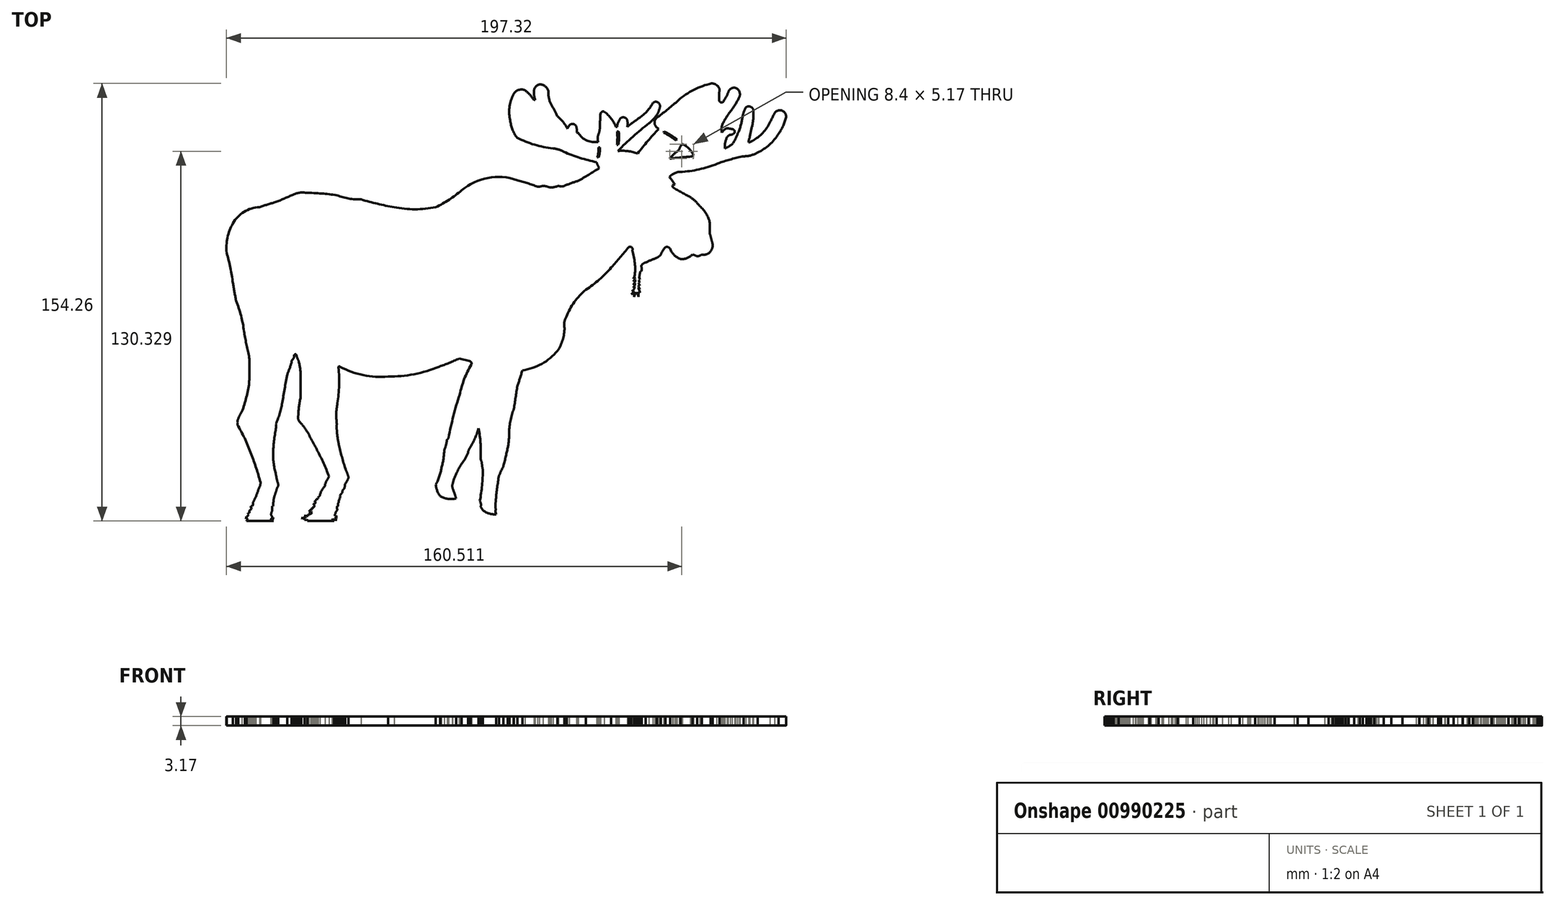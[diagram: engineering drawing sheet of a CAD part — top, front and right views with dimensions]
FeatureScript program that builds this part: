
annotation { "Feature Type Name" : "Feature", "Feature Type Description" : "" }
export const myFeature = defineFeature(function(context is Context, id is Id, definition is map)
    precondition{}
    {
        {
            var Q0;
            Q0=qCreatedBy(makeId("Top.planeOp"),FACE);
            var sketch = newSketch(context, id + "F0", { "sketchPlane" : qUnion([Q0])});
            skArc(sketch, "E0", {"start": v(147.27, 120.2) * mm, "mid": v(137.02, 120.96) * mm, "end": v(127.73, 116.58) * mm});
            skArc(sketch, "E1", {"start": v(118.62, 110.64) * mm, "mid": v(123.37, 113.31) * mm, "end": v(127.73, 116.58) * mm});
            skArc(sketch, "E2", {"start": v(103.93, 110.64) * mm, "mid": v(111.28, 109.9) * mm, "end": v(118.62, 110.64) * mm});
            skArc(sketch, "E3", {"start": v(92.29, 113.4) * mm, "mid": v(98.07, 111.84) * mm, "end": v(103.93, 110.64) * mm});
            skArc(sketch, "E4", {"start": v(83.82, 114.84) * mm, "mid": v(87.98, 113.66) * mm, "end": v(92.29, 113.4) * mm});
            skArc(sketch, "E5", {"start": v(83.82, 114.84) * mm, "mid": v(78.38, 115.45) * mm, "end": v(72.9, 115.7) * mm});
            skArc(sketch, "E6", {"start": v(72.9, 115.7) * mm, "mid": v(70.3, 115.7) * mm, "end": v(67.84, 114.84) * mm});
            skArc(sketch, "E7", {"start": v(61.98, 112.38) * mm, "mid": v(64.93, 113.56) * mm, "end": v(67.84, 114.84) * mm});
            skArc(sketch, "E8", {"start": v(61.98, 112.38) * mm, "mid": v(59.21, 111.56) * mm, "end": v(56.48, 110.64) * mm});
            skArc(sketch, "E9", {"start": v(56.48, 110.64) * mm, "mid": v(51.05, 109) * mm, "end": v(47.1, 104.92) * mm});
            skArc(sketch, "E10", {"start": v(47.1, 104.92) * mm, "mid": v(45.23, 99.89) * mm, "end": v(44.92, 94.53) * mm});
            skArc(sketch, "E11", {"start": v(47.1, 83.95) * mm, "mid": v(46.2, 89.28) * mm, "end": v(44.92, 94.53) * mm});
            skArc(sketch, "E12", {"start": v(47.1, 83.95) * mm, "mid": v(47.65, 80.8) * mm, "end": v(48.2, 77.66) * mm});
            skArc(sketch, "E13", {"start": v(51.03, 66.86) * mm, "mid": v(49.97, 72.36) * mm, "end": v(48.2, 77.66) * mm});
            skArc(sketch, "E14", {"start": v(51.03, 66.86) * mm, "mid": v(51.84, 62.51) * mm, "end": v(52.85, 58.2) * mm});
            skArc(sketch, "E15", {"start": v(52.85, 48.63) * mm, "mid": v(52.95, 53.42) * mm, "end": v(52.85, 58.2) * mm});
            skArc(sketch, "E16", {"start": v(50.3, 38.56) * mm, "mid": v(51.84, 43.53) * mm, "end": v(52.85, 48.63) * mm});
            skArc(sketch, "E17", {"start": v(50.3, 38.56) * mm, "mid": v(49.54, 37.31) * mm, "end": v(48.98, 35.96) * mm});
            skArc(sketch, "E18", {"start": v(48.98, 35.96) * mm, "mid": v(48.68, 34.67) * mm, "end": v(48.98, 33.37) * mm});
            skArc(sketch, "E19", {"start": v(53.58, 23.48) * mm, "mid": v(51.53, 28.54) * mm, "end": v(48.98, 33.37) * mm});
            skArc(sketch, "E20", {"start": v(56.82, 13.59) * mm, "mid": v(55.35, 18.58) * mm, "end": v(53.58, 23.48) * mm});
            skArc(sketch, "E21", {"start": v(56.48, 11.9) * mm, "mid": v(56.77, 12.72) * mm, "end": v(56.82, 13.59) * mm});
            skArc(sketch, "E22", {"start": v(56.48, 11.9) * mm, "mid": v(55.79, 10.14) * mm, "end": v(55.2, 8.34) * mm});
            skLineSegment(sketch, "E23", {"start": v(55.2, 8.34) * mm, "end": v(54.71, 7.8) * mm});
            skLineSegment(sketch, "E24", {"start": v(54.71, 7.8) * mm, "end": v(54.71, 7.32) * mm});
            skLineSegment(sketch, "E25", {"start": v(54.71, 7.32) * mm, "end": v(54.14, 6.57) * mm});
            skLineSegment(sketch, "E26", {"start": v(54.14, 6.57) * mm, "end": v(54.14, 6.18) * mm});
            skLineSegment(sketch, "E27", {"start": v(54.14, 6.18) * mm, "end": v(54.14, 5.68) * mm});
            skLineSegment(sketch, "E28", {"start": v(54.14, 5.68) * mm, "end": v(53.9, 5.27) * mm});
            skLineSegment(sketch, "E29", {"start": v(53.9, 5.27) * mm, "end": v(53.4, 5.27) * mm});
            skLineSegment(sketch, "E30", {"start": v(53.4, 5.27) * mm, "end": v(53.4, 5) * mm});
            skLineSegment(sketch, "E31", {"start": v(53.4, 5) * mm, "end": v(53.73, 4.26) * mm});
            skLineSegment(sketch, "E32", {"start": v(53.73, 4.26) * mm, "end": v(52.96, 3.72) * mm});
            skLineSegment(sketch, "E33", {"start": v(52.96, 3.72) * mm, "end": v(52.96, 2.8) * mm});
            skLineSegment(sketch, "E34", {"start": v(52.96, 2.8) * mm, "end": v(52.48, 2.8) * mm});
            skLineSegment(sketch, "E35", {"start": v(52.48, 2.8) * mm, "end": v(52.4, 2.5) * mm});
            skLineSegment(sketch, "E36", {"start": v(52.4, 2.5) * mm, "end": v(52.65, 2.15) * mm});
            skLineSegment(sketch, "E37", {"start": v(52.65, 2.15) * mm, "end": v(52.29, 1.8) * mm});
            skLineSegment(sketch, "E38", {"start": v(52.29, 1.8) * mm, "end": v(52.01, 1.59) * mm});
            skLineSegment(sketch, "E39", {"start": v(52.01, 1.59) * mm, "end": v(51.87, 1.1) * mm});
            skLineSegment(sketch, "E40", {"start": v(51.87, 1.1) * mm, "end": v(51.47, 1.1) * mm});
            skLineSegment(sketch, "E41", {"start": v(51.47, 1.1) * mm, "end": v(52.12, 0.85) * mm});
            skLineSegment(sketch, "E42", {"start": v(52.12, 0.85) * mm, "end": v(52.12, 0.4) * mm});
            skLineSegment(sketch, "E43", {"start": v(52.12, 0.4) * mm, "end": v(52.04, 0.2) * mm});
            skLineSegment(sketch, "E44", {"start": v(52.04, 0.2) * mm, "end": v(51.86, 0.2) * mm});
            skLineSegment(sketch, "E45", {"start": v(51.86, 0.2) * mm, "end": v(51.86, 0) * mm});
            skLineSegment(sketch, "E46", {"start": v(51.86, 0) * mm, "end": v(61.45, 0) * mm});
            skLineSegment(sketch, "E47", {"start": v(61.45, 0) * mm, "end": v(60.66, 0.2) * mm});
            skArc(sketch, "E48", {"start": v(60.86, 0.86) * mm, "mid": v(60.5, 0.6) * mm, "end": v(60.66, 0.2) * mm});
            skArc(sketch, "E49", {"start": v(60.86, 0.86) * mm, "mid": v(61.23, 0.8) * mm, "end": v(61.6, 0.77) * mm});
            skArc(sketch, "E50", {"start": v(61.6, 0.77) * mm, "mid": v(61.3, 1) * mm, "end": v(61, 1.21) * mm});
            skArc(sketch, "E51", {"start": v(60.86, 1.81) * mm, "mid": v(60.9, 1.5) * mm, "end": v(61, 1.21) * mm});
            skArc(sketch, "E52", {"start": v(60.66, 1.89) * mm, "mid": v(60.75, 1.81) * mm, "end": v(60.86, 1.81) * mm});
            skArc(sketch, "E53", {"start": v(61, 3.62) * mm, "mid": v(60.65, 2.79) * mm, "end": v(60.66, 1.89) * mm});
            skArc(sketch, "E54", {"start": v(61, 5.23) * mm, "mid": v(60.98, 4.42) * mm, "end": v(61, 3.62) * mm});
            skArc(sketch, "E55", {"start": v(61.6, 8.16) * mm, "mid": v(61.39, 6.7) * mm, "end": v(61.38, 5.23) * mm});
            skLineSegment(sketch, "E56", {"start": v(61.38, 5.23) * mm, "end": v(61, 5.23) * mm});
            skArc(sketch, "E57", {"start": v(62.5, 10.85) * mm, "mid": v(62.03, 9.51) * mm, "end": v(61.6, 8.16) * mm});
            skArc(sketch, "E58", {"start": v(63.08, 12.3) * mm, "mid": v(62.73, 11.68) * mm, "end": v(62.5, 11.02) * mm});
            skLineSegment(sketch, "E59", {"start": v(62.5, 10.85) * mm, "end": v(62.5, 11.02) * mm});
            skArc(sketch, "E60", {"start": v(63.08, 12.3) * mm, "mid": v(63.1, 12.9) * mm, "end": v(62.91, 13.49) * mm});
            skArc(sketch, "E61", {"start": v(62.27, 16.4) * mm, "mid": v(62.55, 14.93) * mm, "end": v(62.91, 13.49) * mm});
            skArc(sketch, "E62", {"start": v(61.27, 23.8) * mm, "mid": v(61.52, 20.06) * mm, "end": v(62.27, 16.4) * mm});
            skArc(sketch, "E63", {"start": v(62.27, 32.62) * mm, "mid": v(61.63, 28.22) * mm, "end": v(61.27, 23.8) * mm});
            skArc(sketch, "E64", {"start": v(62.27, 32.62) * mm, "mid": v(62.34, 33.38) * mm, "end": v(62.27, 34.14) * mm});
            skArc(sketch, "E65", {"start": v(62.27, 34.14) * mm, "mid": v(63.6, 37.84) * mm, "end": v(64.5, 41.66) * mm});
            skArc(sketch, "E66", {"start": v(66.24, 51.53) * mm, "mid": v(65.35, 46.6) * mm, "end": v(64.5, 41.66) * mm});
            skArc(sketch, "E67", {"start": v(66.24, 51.53) * mm, "mid": v(67.04, 53.64) * mm, "end": v(67.79, 55.77) * mm});
            skArc(sketch, "E68", {"start": v(67.79, 56.5) * mm, "mid": v(67.76, 56.13) * mm, "end": v(67.79, 55.77) * mm});
            skArc(sketch, "E69", {"start": v(67.79, 56.5) * mm, "mid": v(68.25, 57.03) * mm, "end": v(68.65, 57.61) * mm});
            skArc(sketch, "E70", {"start": v(69.43, 58.68) * mm, "mid": v(68.92, 58.7) * mm, "end": v(68.7, 58.25) * mm});
            skArc(sketch, "E71", {"start": v(68.7, 58.25) * mm, "mid": v(68.63, 57.93) * mm, "end": v(68.65, 57.61) * mm});
            skArc(sketch, "E72", {"start": v(69.43, 58.68) * mm, "mid": v(69.81, 57.5) * mm, "end": v(70.3, 56.38) * mm});
            skArc(sketch, "E73", {"start": v(71.02, 50.46) * mm, "mid": v(70.86, 53.44) * mm, "end": v(70.3, 56.38) * mm});
            skLineSegment(sketch, "E74", {"start": v(71.02, 50.46) * mm, "end": v(71.02, 43.72) * mm});
            skArc(sketch, "E75", {"start": v(71.02, 43.72) * mm, "mid": v(70.44, 40.5) * mm, "end": v(70.15, 37.25) * mm});
            skArc(sketch, "E76", {"start": v(70.15, 37.25) * mm, "mid": v(70.1, 36.07) * mm, "end": v(70.62, 35) * mm});
            skArc(sketch, "E77", {"start": v(72.94, 32.1) * mm, "mid": v(71.84, 33.6) * mm, "end": v(70.62, 35) * mm});
            skArc(sketch, "E78", {"start": v(76.86, 24.83) * mm, "mid": v(74.95, 28.5) * mm, "end": v(72.94, 32.1) * mm});
            skArc(sketch, "E79", {"start": v(80.96, 15.74) * mm, "mid": v(79.08, 20.36) * mm, "end": v(76.86, 24.83) * mm});
            skArc(sketch, "E80", {"start": v(79.55, 12.91) * mm, "mid": v(80.27, 14.32) * mm, "end": v(80.96, 15.74) * mm});
            skArc(sketch, "E81", {"start": v(79.64, 12.32) * mm, "mid": v(78.43, 10.81) * mm, "end": v(77.77, 9) * mm});
            skLineSegment(sketch, "E82", {"start": v(79.64, 12.32) * mm, "end": v(79.55, 12.91) * mm});
            skArc(sketch, "E83", {"start": v(77.08, 8.3) * mm, "mid": v(77.5, 8.59) * mm, "end": v(77.77, 9) * mm});
            skArc(sketch, "E84", {"start": v(76.55, 7.75) * mm, "mid": v(76.86, 7.7) * mm, "end": v(77.17, 7.78) * mm});
            skArc(sketch, "E85", {"start": v(75.82, 6.86) * mm, "mid": v(76.32, 7.2) * mm, "end": v(76.55, 7.75) * mm});
            skArc(sketch, "E86", {"start": v(76.24, 6.51) * mm, "mid": v(76.08, 6.74) * mm, "end": v(75.82, 6.86) * mm});
            skArc(sketch, "E87", {"start": v(75.45, 6) * mm, "mid": v(75.96, 6.08) * mm, "end": v(76.24, 6.51) * mm});
            skArc(sketch, "E88", {"start": v(75.82, 5.35) * mm, "mid": v(75.7, 5.72) * mm, "end": v(75.45, 6) * mm});
            skArc(sketch, "E89", {"start": v(75.45, 4.72) * mm, "mid": v(75.76, 4.96) * mm, "end": v(75.82, 5.35) * mm});
            skArc(sketch, "E90", {"start": v(74.98, 4.72) * mm, "mid": v(75.21, 4.64) * mm, "end": v(75.45, 4.72) * mm});
            skArc(sketch, "E91", {"start": v(74.98, 4.06) * mm, "mid": v(75.07, 4.4) * mm, "end": v(74.98, 4.72) * mm});
            skLineSegment(sketch, "E92", {"start": v(74.98, 4.06) * mm, "end": v(74.47, 3.96) * mm});
            skLineSegment(sketch, "E93", {"start": v(74.47, 3.96) * mm, "end": v(73.9, 3.36) * mm});
            skLineSegment(sketch, "E94", {"start": v(73.9, 3.36) * mm, "end": v(74.81, 3.22) * mm});
            skLineSegment(sketch, "E95", {"start": v(74.81, 3.22) * mm, "end": v(74.98, 2.88) * mm});
            skLineSegment(sketch, "E96", {"start": v(74.98, 2.88) * mm, "end": v(74.73, 2.66) * mm});
            skLineSegment(sketch, "E97", {"start": v(74.73, 2.66) * mm, "end": v(74.47, 2.4) * mm});
            skLineSegment(sketch, "E98", {"start": v(74.47, 2.4) * mm, "end": v(73.82, 2.4) * mm});
            skLineSegment(sketch, "E99", {"start": v(73.82, 2.4) * mm, "end": v(73.58, 1.75) * mm});
            skLineSegment(sketch, "E100", {"start": v(73.58, 1.75) * mm, "end": v(73.07, 1.75) * mm});
            skLineSegment(sketch, "E101", {"start": v(73.07, 1.75) * mm, "end": v(72.27, 1.75) * mm});
            skLineSegment(sketch, "E102", {"start": v(72.27, 1.75) * mm, "end": v(72.92, 1.26) * mm});
            skLineSegment(sketch, "E103", {"start": v(72.92, 1.26) * mm, "end": v(72.75, 1.04) * mm});
            skLineSegment(sketch, "E104", {"start": v(72.75, 1.04) * mm, "end": v(72.34, 1.09) * mm});
            skLineSegment(sketch, "E105", {"start": v(72.34, 1.09) * mm, "end": v(71.3, 1.09) * mm});
            skLineSegment(sketch, "E106", {"start": v(71.3, 1.09) * mm, "end": v(72.43, 0.71) * mm});
            skLineSegment(sketch, "E107", {"start": v(72.43, 0.71) * mm, "end": v(72.43, 0.45) * mm});
            skLineSegment(sketch, "E108", {"start": v(72.43, 0.45) * mm, "end": v(73.6, 0.28) * mm});
            skLineSegment(sketch, "E109", {"start": v(73.6, 0.28) * mm, "end": v(73.4, 0) * mm});
            skLineSegment(sketch, "E110", {"start": v(73.4, 0) * mm, "end": v(82.74, 0) * mm});
            skLineSegment(sketch, "E111", {"start": v(77.17, 7.78) * mm, "end": v(77.08, 8.3) * mm});
            skLineSegment(sketch, "E112", {"start": v(82.74, 0) * mm, "end": v(82.13, 0.2) * mm});
            skLineSegment(sketch, "E113", {"start": v(82.13, 0.2) * mm, "end": v(81.98, 0.38) * mm});
            skLineSegment(sketch, "E114", {"start": v(81.98, 0.38) * mm, "end": v(82.29, 0.63) * mm});
            skLineSegment(sketch, "E115", {"start": v(82.29, 0.63) * mm, "end": v(82.95, 0.42) * mm});
            skLineSegment(sketch, "E116", {"start": v(82.95, 0.42) * mm, "end": v(83.3, 0.42) * mm});
            skLineSegment(sketch, "E117", {"start": v(83.3, 0.42) * mm, "end": v(83.78, 0.42) * mm});
            skLineSegment(sketch, "E118", {"start": v(83.78, 0.42) * mm, "end": v(83.26, 0.64) * mm});
            skLineSegment(sketch, "E119", {"start": v(83.26, 0.64) * mm, "end": v(83.26, 1.24) * mm});
            skLineSegment(sketch, "E120", {"start": v(83.26, 1.24) * mm, "end": v(83.86, 1.36) * mm});
            skLineSegment(sketch, "E121", {"start": v(83.86, 1.36) * mm, "end": v(83.43, 1.61) * mm});
            skLineSegment(sketch, "E122", {"start": v(83.43, 1.61) * mm, "end": v(83.13, 1.8) * mm});
            skLineSegment(sketch, "E123", {"start": v(83.13, 1.8) * mm, "end": v(83.03, 2.12) * mm});
            skLineSegment(sketch, "E124", {"start": v(83.03, 2.12) * mm, "end": v(83.07, 2.32) * mm});
            skLineSegment(sketch, "E125", {"start": v(83.07, 2.32) * mm, "end": v(83.33, 2.55) * mm});
            skLineSegment(sketch, "E126", {"start": v(83.33, 2.55) * mm, "end": v(83.33, 3.08) * mm});
            skLineSegment(sketch, "E127", {"start": v(83.33, 3.08) * mm, "end": v(83.98, 3.88) * mm});
            skArc(sketch, "E128", {"start": v(83.8, 5.06) * mm, "mid": v(83.8, 4.46) * mm, "end": v(83.98, 3.88) * mm});
            skArc(sketch, "E129", {"start": v(84.27, 5.29) * mm, "mid": v(84.01, 5.22) * mm, "end": v(83.8, 5.06) * mm});
            skArc(sketch, "E130", {"start": v(84.5, 6.68) * mm, "mid": v(84.17, 6.02) * mm, "end": v(84.27, 5.29) * mm});
            skArc(sketch, "E131", {"start": v(84.7, 7.61) * mm, "mid": v(84.48, 7.17) * mm, "end": v(84.5, 6.68) * mm});
            skArc(sketch, "E132", {"start": v(84.5, 7.83) * mm, "mid": v(84.83, 8.1) * mm, "end": v(85.08, 8.43) * mm});
            skArc(sketch, "E133", {"start": v(84.75, 8.9) * mm, "mid": v(85.25, 9.44) * mm, "end": v(85.69, 10.03) * mm});
            skLineSegment(sketch, "E134", {"start": v(84.7, 7.61) * mm, "end": v(84.5, 7.83) * mm});
            skLineSegment(sketch, "E135", {"start": v(85.08, 8.43) * mm, "end": v(84.75, 8.9) * mm});
            skArc(sketch, "E136", {"start": v(86.05, 11.12) * mm, "mid": v(85.75, 10.6) * mm, "end": v(85.69, 10.03) * mm});
            skArc(sketch, "E137", {"start": v(86.05, 11.12) * mm, "mid": v(86.33, 11.38) * mm, "end": v(86.45, 11.76) * mm});
            skArc(sketch, "E138", {"start": v(86.45, 11.76) * mm, "mid": v(86.62, 12.37) * mm, "end": v(86.65, 13.01) * mm});
            skArc(sketch, "E139", {"start": v(86.65, 13.01) * mm, "mid": v(87.39, 14.17) * mm, "end": v(87.91, 15.44) * mm});
            skArc(sketch, "E140", {"start": v(87.91, 15.44) * mm, "mid": v(87.37, 16.9) * mm, "end": v(86.8, 18.34) * mm});
            skArc(sketch, "E141", {"start": v(84.45, 27) * mm, "mid": v(85.53, 22.64) * mm, "end": v(86.8, 18.34) * mm});
            skArc(sketch, "E142", {"start": v(83.77, 32.01) * mm, "mid": v(84, 29.5) * mm, "end": v(84.45, 27) * mm});
            skArc(sketch, "E143", {"start": v(83.77, 34.2) * mm, "mid": v(83.65, 33.1) * mm, "end": v(83.77, 32.01) * mm});
            skArc(sketch, "E144", {"start": v(83.55, 38.12) * mm, "mid": v(83.59, 36.15) * mm, "end": v(83.77, 34.2) * mm});
            skArc(sketch, "E145", {"start": v(83.97, 41.5) * mm, "mid": v(83.72, 39.82) * mm, "end": v(83.55, 38.12) * mm});
            skArc(sketch, "E146", {"start": v(83.97, 41.5) * mm, "mid": v(84.55, 47.77) * mm, "end": v(84.33, 54.05) * mm});
            skArc(sketch, "E147", {"start": v(84.82, 54.41) * mm, "mid": v(84.42, 54.45) * mm, "end": v(84.33, 54.05) * mm});
            skArc(sketch, "E148", {"start": v(84.82, 54.41) * mm, "mid": v(93.08, 51.4) * mm, "end": v(101.86, 50.91) * mm});
            skArc(sketch, "E149", {"start": v(101.86, 50.91) * mm, "mid": v(111.02, 51.74) * mm, "end": v(119.83, 54.41) * mm});
            skArc(sketch, "E150", {"start": v(119.83, 54.41) * mm, "mid": v(123.38, 55.75) * mm, "end": v(126.85, 57.27) * mm});
            skLineSegment(sketch, "E151", {"start": v(126.85, 57.27) * mm, "end": v(130.57, 56.37) * mm});
            skArc(sketch, "E152", {"start": v(131.15, 55.1) * mm, "mid": v(131.17, 55.88) * mm, "end": v(130.57, 56.37) * mm});
            skArc(sketch, "E153", {"start": v(131.15, 55.1) * mm, "mid": v(128.68, 50) * mm, "end": v(127.05, 44.56) * mm});
            skArc(sketch, "E154", {"start": v(127.05, 44.56) * mm, "mid": v(124.85, 37.02) * mm, "end": v(123.14, 29.35) * mm});
            skArc(sketch, "E155", {"start": v(121.64, 25) * mm, "mid": v(122.24, 26.8) * mm, "end": v(122.61, 28.67) * mm});
            skArc(sketch, "E156", {"start": v(120.7, 18.85) * mm, "mid": v(121.33, 21.9) * mm, "end": v(121.64, 25) * mm});
            skArc(sketch, "E157", {"start": v(122.61, 28.67) * mm, "mid": v(122.93, 28.97) * mm, "end": v(123.14, 29.35) * mm});
            skArc(sketch, "E158", {"start": v(118.64, 12.8) * mm, "mid": v(119.91, 15.74) * mm, "end": v(120.7, 18.85) * mm});
            skArc(sketch, "E159", {"start": v(118.64, 12.8) * mm, "mid": v(119.14, 10.62) * mm, "end": v(120.25, 8.67) * mm});
            skArc(sketch, "E160", {"start": v(120.25, 8.67) * mm, "mid": v(122.94, 7.77) * mm, "end": v(125.78, 7.93) * mm});
            skArc(sketch, "E161", {"start": v(125.78, 7.93) * mm, "mid": v(125.28, 9.57) * mm, "end": v(124.7, 11.18) * mm});
            skArc(sketch, "E162", {"start": v(124.53, 13.02) * mm, "mid": v(124.48, 12.1) * mm, "end": v(124.7, 11.18) * mm});
            skArc(sketch, "E163", {"start": v(127.73, 20.17) * mm, "mid": v(125.88, 16.7) * mm, "end": v(124.53, 13.02) * mm});
            skArc(sketch, "E164", {"start": v(127.73, 20.17) * mm, "mid": v(129.02, 22) * mm, "end": v(129.98, 24.04) * mm});
            skArc(sketch, "E165", {"start": v(130.92, 26.14) * mm, "mid": v(130.34, 25.14) * mm, "end": v(129.98, 24.04) * mm});
            skArc(sketch, "E166", {"start": v(130.92, 26.14) * mm, "mid": v(132.54, 29.31) * mm, "end": v(133.77, 32.66) * mm});
            skArc(sketch, "E167", {"start": v(134.45, 22.58) * mm, "mid": v(134.4, 27.64) * mm, "end": v(133.77, 32.66) * mm});
            skArc(sketch, "E168", {"start": v(134.45, 22.58) * mm, "mid": v(134.52, 21.65) * mm, "end": v(134.86, 20.78) * mm});
            skArc(sketch, "E169", {"start": v(134.86, 20.78) * mm, "mid": v(134.98, 19.42) * mm, "end": v(135.23, 18.07) * mm});
            skArc(sketch, "E170", {"start": v(134.15, 7.1) * mm, "mid": v(134.97, 12.55) * mm, "end": v(135.23, 18.07) * mm});
            skArc(sketch, "E171", {"start": v(134.45, 4.93) * mm, "mid": v(134.54, 6.04) * mm, "end": v(134.15, 7.1) * mm});
            skLineSegment(sketch, "E172", {"start": v(134.45, 4.93) * mm, "end": v(135.27, 3.8) * mm});
            skArc(sketch, "E173", {"start": v(135.27, 3.8) * mm, "mid": v(137.43, 2.63) * mm, "end": v(139.88, 2.33) * mm});
            skLineSegment(sketch, "E174", {"start": v(139.88, 2.33) * mm, "end": v(139.62, 3.24) * mm});
            skArc(sketch, "E175", {"start": v(139.62, 3.24) * mm, "mid": v(139.75, 4.1) * mm, "end": v(139.62, 4.95) * mm});
            skArc(sketch, "E176", {"start": v(139.84, 7.68) * mm, "mid": v(139.73, 6.31) * mm, "end": v(139.62, 4.95) * mm});
            skArc(sketch, "E177", {"start": v(140.95, 15.96) * mm, "mid": v(140.28, 11.83) * mm, "end": v(139.84, 7.68) * mm});
            skArc(sketch, "E178", {"start": v(142.43, 19.07) * mm, "mid": v(141.64, 17.54) * mm, "end": v(140.95, 15.96) * mm});
            skArc(sketch, "E179", {"start": v(142.43, 19.07) * mm, "mid": v(143.25, 22.43) * mm, "end": v(144.02, 25.8) * mm});
            skArc(sketch, "E180", {"start": v(144.02, 25.8) * mm, "mid": v(144.4, 28.52) * mm, "end": v(144.53, 31.26) * mm});
            skArc(sketch, "E181", {"start": v(146.2, 39.56) * mm, "mid": v(144.97, 35.49) * mm, "end": v(144.53, 31.26) * mm});
            skArc(sketch, "E182", {"start": v(147.42, 47.62) * mm, "mid": v(146.8, 43.6) * mm, "end": v(146.2, 39.56) * mm});
            skArc(sketch, "E183", {"start": v(147.42, 47.62) * mm, "mid": v(148.34, 50.36) * mm, "end": v(149.15, 53.14) * mm});
            skArc(sketch, "E184", {"start": v(149.15, 53.14) * mm, "mid": v(156, 55.38) * mm, "end": v(161.55, 59.97) * mm});
            skArc(sketch, "E185", {"start": v(161.55, 59.97) * mm, "mid": v(163.4, 63.84) * mm, "end": v(164.01, 68.09) * mm});
            skArc(sketch, "E186", {"start": v(164.7, 71.96) * mm, "mid": v(163.96, 70.1) * mm, "end": v(164.01, 68.09) * mm});
            skArc(sketch, "E187", {"start": v(171.53, 81.48) * mm, "mid": v(167.48, 77.18) * mm, "end": v(164.7, 71.96) * mm});
            skArc(sketch, "E188", {"start": v(171.53, 81.48) * mm, "mid": v(176.29, 85.12) * mm, "end": v(180.5, 89.37) * mm});
            skArc(sketch, "E189", {"start": v(180.5, 89.37) * mm, "mid": v(183.64, 92.92) * mm, "end": v(186.66, 96.57) * mm});
            skArc(sketch, "E190", {"start": v(187.94, 95.43) * mm, "mid": v(187.74, 96.5) * mm, "end": v(186.66, 96.57) * mm});
            skArc(sketch, "E191", {"start": v(188.75, 86.27) * mm, "mid": v(188.83, 90.9) * mm, "end": v(187.94, 95.43) * mm});
            skLineSegment(sketch, "E192", {"start": v(188.75, 86.27) * mm, "end": v(188.3, 85.34) * mm});
            skLineSegment(sketch, "E193", {"start": v(188.3, 85.34) * mm, "end": v(188.75, 85.92) * mm});
            skLineSegment(sketch, "E194", {"start": v(188.75, 85.92) * mm, "end": v(188.98, 85.38) * mm});
            skLineSegment(sketch, "E195", {"start": v(188.98, 85.38) * mm, "end": v(188.31, 84.4) * mm});
            skLineSegment(sketch, "E196", {"start": v(188.31, 84.4) * mm, "end": v(188.98, 84.93) * mm});
            skLineSegment(sketch, "E197", {"start": v(188.98, 84.93) * mm, "end": v(188.98, 84.4) * mm});
            skLineSegment(sketch, "E198", {"start": v(188.98, 84.4) * mm, "end": v(188.22, 83.23) * mm});
            skLineSegment(sketch, "E199", {"start": v(188.22, 83.23) * mm, "end": v(189.02, 83.9) * mm});
            skLineSegment(sketch, "E200", {"start": v(189.02, 83.9) * mm, "end": v(188.75, 82.95) * mm});
            skLineSegment(sketch, "E201", {"start": v(188.75, 82.95) * mm, "end": v(188.15, 82.2) * mm});
            skLineSegment(sketch, "E202", {"start": v(188.15, 82.2) * mm, "end": v(188.75, 82.68) * mm});
            skArc(sketch, "E203", {"start": v(187.8, 81.04) * mm, "mid": v(188.5, 81.73) * mm, "end": v(188.75, 82.68) * mm});
            skArc(sketch, "E204", {"start": v(187.8, 81.04) * mm, "mid": v(188.1, 81.1) * mm, "end": v(188.39, 81.2) * mm});
            skArc(sketch, "E205", {"start": v(187.6, 79.95) * mm, "mid": v(188.1, 80.51) * mm, "end": v(188.39, 81.2) * mm});
            skArc(sketch, "E206", {"start": v(187.6, 79.95) * mm, "mid": v(188.2, 80.28) * mm, "end": v(188.61, 80.82) * mm});
            skArc(sketch, "E207", {"start": v(188.61, 79.04) * mm, "mid": v(188.63, 79.93) * mm, "end": v(188.61, 80.82) * mm});
            skArc(sketch, "E208", {"start": v(189.32, 80.5) * mm, "mid": v(188.88, 79.82) * mm, "end": v(188.61, 79.04) * mm});
            skArc(sketch, "E209", {"start": v(190.1, 79.04) * mm, "mid": v(189.83, 79.84) * mm, "end": v(189.32, 80.5) * mm});
            skArc(sketch, "E210", {"start": v(190.1, 79.04) * mm, "mid": v(190.13, 79.93) * mm, "end": v(190.1, 80.82) * mm});
            skArc(sketch, "E211", {"start": v(190.65, 80.5) * mm, "mid": v(190.4, 80.72) * mm, "end": v(190.1, 80.82) * mm});
            skArc(sketch, "E212", {"start": v(190.65, 80.5) * mm, "mid": v(190.5, 81.09) * mm, "end": v(190.22, 81.61) * mm});
            skLineSegment(sketch, "E213", {"start": v(190.22, 81.61) * mm, "end": v(190.12, 82.12) * mm});
            skLineSegment(sketch, "E214", {"start": v(190.12, 82.12) * mm, "end": v(190.65, 81.72) * mm});
            skLineSegment(sketch, "E215", {"start": v(190.65, 81.72) * mm, "end": v(190.15, 82.59) * mm});
            skLineSegment(sketch, "E216", {"start": v(190.15, 82.59) * mm, "end": v(190.17, 83.02) * mm});
            skLineSegment(sketch, "E217", {"start": v(190.17, 83.02) * mm, "end": v(190.66, 82.95) * mm});
            skLineSegment(sketch, "E218", {"start": v(190.66, 82.95) * mm, "end": v(190.15, 83.9) * mm});
            skLineSegment(sketch, "E219", {"start": v(190.15, 83.9) * mm, "end": v(190.49, 84) * mm});
            skLineSegment(sketch, "E220", {"start": v(190.49, 84) * mm, "end": v(190.25, 84.97) * mm});
            skLineSegment(sketch, "E221", {"start": v(190.25, 84.97) * mm, "end": v(190.61, 85.06) * mm});
            skLineSegment(sketch, "E222", {"start": v(190.61, 85.06) * mm, "end": v(190.38, 86) * mm});
            skArc(sketch, "E223", {"start": v(190.77, 88.06) * mm, "mid": v(190.56, 87.03) * mm, "end": v(190.38, 86) * mm});
            skArc(sketch, "E224", {"start": v(191.16, 88.08) * mm, "mid": v(191.2, 89.07) * mm, "end": v(191.09, 90.04) * mm});
            skLineSegment(sketch, "E225", {"start": v(190.77, 88.06) * mm, "end": v(191.16, 88.08) * mm});
            skArc(sketch, "E226", {"start": v(192.62, 91.14) * mm, "mid": v(191.76, 90.72) * mm, "end": v(191.09, 90.04) * mm});
            skArc(sketch, "E227", {"start": v(196.56, 92.76) * mm, "mid": v(194.57, 92) * mm, "end": v(192.62, 91.14) * mm});
            skArc(sketch, "E228", {"start": v(196.56, 92.76) * mm, "mid": v(197.32, 93.3) * mm, "end": v(198.02, 93.94) * mm});
            skArc(sketch, "E229", {"start": v(199.66, 96.56) * mm, "mid": v(198.7, 95.33) * mm, "end": v(198.02, 93.94) * mm});
            skArc(sketch, "E230", {"start": v(201.27, 95.97) * mm, "mid": v(200.57, 96.55) * mm, "end": v(199.66, 96.56) * mm});
            skArc(sketch, "E231", {"start": v(201.27, 95.97) * mm, "mid": v(202.72, 93.74) * mm, "end": v(204.97, 92.32) * mm});
            skArc(sketch, "E232", {"start": v(204.97, 92.32) * mm, "mid": v(207.22, 92.69) * mm, "end": v(209.14, 93.94) * mm});
            skArc(sketch, "E233", {"start": v(210.75, 93.3) * mm, "mid": v(209.97, 93.7) * mm, "end": v(209.14, 93.94) * mm});
            skArc(sketch, "E234", {"start": v(210.75, 93.3) * mm, "mid": v(211.64, 93.5) * mm, "end": v(212.44, 93.94) * mm});
            skArc(sketch, "E235", {"start": v(212.44, 93.94) * mm, "mid": v(214.26, 94.06) * mm, "end": v(215.68, 95.22) * mm});
            skArc(sketch, "E236", {"start": v(215.68, 95.22) * mm, "mid": v(216.25, 96.82) * mm, "end": v(216, 98.5) * mm});
            skArc(sketch, "E237", {"start": v(216, 98.5) * mm, "mid": v(215.67, 99.85) * mm, "end": v(215.29, 101.19) * mm});
            skArc(sketch, "E238", {"start": v(215.29, 105.13) * mm, "mid": v(215.24, 103.16) * mm, "end": v(215.29, 101.19) * mm});
            skArc(sketch, "E239", {"start": v(215.29, 105.13) * mm, "mid": v(213.98, 108.37) * mm, "end": v(211.71, 111.03) * mm});
            skArc(sketch, "E240", {"start": v(211.71, 111.03) * mm, "mid": v(210.15, 112.73) * mm, "end": v(208.36, 114.17) * mm});
            skArc(sketch, "E241", {"start": v(202.28, 117.6) * mm, "mid": v(205.28, 115.82) * mm, "end": v(208.36, 114.17) * mm});
            skArc(sketch, "E242", {"start": v(202.89, 118.66) * mm, "mid": v(202, 120) * mm, "end": v(201.02, 121.25) * mm});
            skLineSegment(sketch, "E243", {"start": v(202.89, 118.66) * mm, "end": v(202.02, 118.4) * mm});
            skLineSegment(sketch, "E244", {"start": v(202.02, 118.4) * mm, "end": v(202.28, 117.6) * mm});
            skArc(sketch, "E245", {"start": v(205.64, 123.1) * mm, "mid": v(203.1, 122.74) * mm, "end": v(201.02, 121.25) * mm});
            skArc(sketch, "E246", {"start": v(205.64, 123.1) * mm, "mid": v(212.28, 124.17) * mm, "end": v(218.68, 126.27) * mm});
            skArc(sketch, "E247", {"start": v(227.2, 128.6) * mm, "mid": v(222.9, 127.57) * mm, "end": v(218.68, 126.27) * mm});
            skArc(sketch, "E248", {"start": v(227.2, 128.6) * mm, "mid": v(229.75, 128.92) * mm, "end": v(232.12, 129.91) * mm});
            skArc(sketch, "E249", {"start": v(232.12, 129.91) * mm, "mid": v(236.3, 132.67) * mm, "end": v(239.5, 136.52) * mm});
            skArc(sketch, "E250", {"start": v(239.5, 136.52) * mm, "mid": v(241.1, 139.34) * mm, "end": v(242.15, 142.4) * mm});
            skArc(sketch, "E251", {"start": v(242.15, 142.4) * mm, "mid": v(240.73, 144.68) * mm, "end": v(238.16, 143.9) * mm});
            skArc(sketch, "E252", {"start": v(238.16, 143.9) * mm, "mid": v(237.32, 142.25) * mm, "end": v(236.5, 140.6) * mm});
            skArc(sketch, "E253", {"start": v(230.32, 134.04) * mm, "mid": v(233.91, 136.84) * mm, "end": v(236.5, 140.6) * mm});
            skArc(sketch, "E254", {"start": v(228.9, 133.49) * mm, "mid": v(229.64, 133.7) * mm, "end": v(230.32, 134.04) * mm});
            skArc(sketch, "E255", {"start": v(229.3, 135.08) * mm, "mid": v(229, 134.3) * mm, "end": v(228.9, 133.49) * mm});
            skArc(sketch, "E256", {"start": v(230.32, 139.9) * mm, "mid": v(229.76, 137.5) * mm, "end": v(229.3, 135.08) * mm});
            skArc(sketch, "E257", {"start": v(230.32, 139.9) * mm, "mid": v(230.62, 142.17) * mm, "end": v(230.64, 144.47) * mm});
            skArc(sketch, "E258", {"start": v(230.64, 144.47) * mm, "mid": v(229.69, 146.03) * mm, "end": v(227.88, 145.75) * mm});
            skArc(sketch, "E259", {"start": v(227.88, 145.75) * mm, "mid": v(227.15, 143.95) * mm, "end": v(226.72, 142.06) * mm});
            skArc(sketch, "E260", {"start": v(225.06, 136.47) * mm, "mid": v(226.1, 139.2) * mm, "end": v(226.72, 142.06) * mm});
            skArc(sketch, "E261", {"start": v(223.14, 132.87) * mm, "mid": v(224.23, 134.6) * mm, "end": v(225.06, 136.47) * mm});
            skArc(sketch, "E262", {"start": v(220.61, 131.37) * mm, "mid": v(221.94, 132.02) * mm, "end": v(223.14, 132.87) * mm});
            skArc(sketch, "E263", {"start": v(221.36, 135.34) * mm, "mid": v(220.66, 133.41) * mm, "end": v(220.61, 131.37) * mm});
            skArc(sketch, "E264", {"start": v(222.53, 136.18) * mm, "mid": v(221.87, 135.87) * mm, "end": v(221.36, 135.34) * mm});
            skArc(sketch, "E265", {"start": v(222.53, 136.18) * mm, "mid": v(223.37, 136.37) * mm, "end": v(224.03, 136.93) * mm});
            skArc(sketch, "E266", {"start": v(224.03, 136.93) * mm, "mid": v(223.86, 137.78) * mm, "end": v(223.1, 138.18) * mm});
            skArc(sketch, "E267", {"start": v(223.1, 138.18) * mm, "mid": v(222.25, 138.33) * mm, "end": v(221.41, 138.48) * mm});
            skArc(sketch, "E268", {"start": v(221.41, 138.48) * mm, "mid": v(220.3, 137.9) * mm, "end": v(219.52, 136.93) * mm});
            skArc(sketch, "E269", {"start": v(219.7, 139.82) * mm, "mid": v(219.36, 138.4) * mm, "end": v(219.52, 136.93) * mm});
            skArc(sketch, "E270", {"start": v(223.1, 145.12) * mm, "mid": v(221.24, 142.57) * mm, "end": v(219.7, 139.82) * mm});
            skArc(sketch, "E271", {"start": v(223.1, 145.12) * mm, "mid": v(224.46, 147.26) * mm, "end": v(225.7, 149.48) * mm});
            skArc(sketch, "E272", {"start": v(225.7, 149.48) * mm, "mid": v(225.72, 151.33) * mm, "end": v(224.44, 152.67) * mm});
            skArc(sketch, "E273", {"start": v(224.44, 152.67) * mm, "mid": v(222.74, 152.47) * mm, "end": v(221.74, 151.09) * mm});
            skArc(sketch, "E274", {"start": v(220.25, 148.28) * mm, "mid": v(221.07, 149.64) * mm, "end": v(221.74, 151.09) * mm});
            skArc(sketch, "E275", {"start": v(218.55, 148.28) * mm, "mid": v(219.4, 147.57) * mm, "end": v(220.25, 148.28) * mm});
            skArc(sketch, "E276", {"start": v(218.64, 151.4) * mm, "mid": v(218.49, 149.84) * mm, "end": v(218.55, 148.28) * mm});
            skArc(sketch, "E277", {"start": v(218.64, 151.4) * mm, "mid": v(218.5, 152.7) * mm, "end": v(217.63, 153.68) * mm});
            skArc(sketch, "E278", {"start": v(217.63, 153.68) * mm, "mid": v(216.82, 154.14) * mm, "end": v(215.9, 154.26) * mm});
            skArc(sketch, "E279", {"start": v(215.9, 154.26) * mm, "mid": v(209.61, 152.05) * mm, "end": v(204.12, 148.28) * mm});
            skArc(sketch, "E280", {"start": v(196.96, 142.46) * mm, "mid": v(200.6, 145.3) * mm, "end": v(204.12, 148.28) * mm});
            skArc(sketch, "E281", {"start": v(196.96, 142.46) * mm, "mid": v(195.78, 140.47) * mm, "end": v(196.96, 138.48) * mm});
            skArc(sketch, "E282", {"start": v(197.23, 138.18) * mm, "mid": v(193.4, 134) * mm, "end": v(189.85, 129.57) * mm});
            skArc(sketch, "E283", {"start": v(204.47, 130.87) * mm, "mid": v(202.7, 129.42) * mm, "end": v(201.15, 127.75) * mm});
            skArc(sketch, "E284", {"start": v(205.62, 132.91) * mm, "mid": v(204.86, 132) * mm, "end": v(204.47, 130.87) * mm});
            skArc(sketch, "E285", {"start": v(209.55, 128.86) * mm, "mid": v(207.96, 131.25) * mm, "end": v(205.62, 132.91) * mm});
            skArc(sketch, "E286", {"start": v(209.15, 128.52) * mm, "mid": v(205.15, 128.18) * mm, "end": v(201.15, 127.75) * mm});
            skLineSegment(sketch, "E287", {"start": v(209.15, 128.52) * mm, "end": v(209.55, 128.86) * mm});
            skLineSegment(sketch, "E288", {"start": v(197.23, 138.18) * mm, "end": v(196.96, 138.48) * mm});
            skArc(sketch, "E289", {"start": v(189.85, 129.57) * mm, "mid": v(186.4, 130.4) * mm, "end": v(182.86, 130.46) * mm});
            skArc(sketch, "E290", {"start": v(193.83, 140.22) * mm, "mid": v(188.17, 135.54) * mm, "end": v(182.86, 130.46) * mm});
            skArc(sketch, "E291", {"start": v(193.83, 140.22) * mm, "mid": v(195.45, 141.76) * mm, "end": v(196.83, 143.53) * mm});
            skArc(sketch, "E292", {"start": v(196.83, 143.53) * mm, "mid": v(197.35, 144.8) * mm, "end": v(197.7, 146.15) * mm});
            skArc(sketch, "E293", {"start": v(197.7, 146.15) * mm, "mid": v(196.88, 147.65) * mm, "end": v(195.19, 147.42) * mm});
            skArc(sketch, "E294", {"start": v(191.08, 142.61) * mm, "mid": v(193.39, 144.8) * mm, "end": v(195.19, 147.42) * mm});
            skArc(sketch, "E295", {"start": v(191.08, 142.61) * mm, "mid": v(188.6, 140.85) * mm, "end": v(186.16, 139.01) * mm});
            skArc(sketch, "E296", {"start": v(186.16, 139.01) * mm, "mid": v(186.3, 140.06) * mm, "end": v(186.16, 141.11) * mm});
            skArc(sketch, "E297", {"start": v(186.16, 141.11) * mm, "mid": v(185.05, 142.31) * mm, "end": v(183.54, 141.68) * mm});
            skArc(sketch, "E298", {"start": v(183.54, 141.68) * mm, "mid": v(182.9, 140.4) * mm, "end": v(182.54, 139.01) * mm});
            skArc(sketch, "E299", {"start": v(182.15, 139.01) * mm, "mid": v(180.46, 141.91) * mm, "end": v(178.08, 144.28) * mm});
            skLineSegment(sketch, "E300", {"start": v(182.54, 139.01) * mm, "end": v(182.15, 139.01) * mm});
            skArc(sketch, "E301", {"start": v(178.08, 144.28) * mm, "mid": v(177.23, 144.27) * mm, "end": v(176.7, 143.6) * mm});
            skArc(sketch, "E302", {"start": v(176.7, 143.6) * mm, "mid": v(176.58, 141.27) * mm, "end": v(176.52, 138.93) * mm});
            skArc(sketch, "E303", {"start": v(175.9, 136.1) * mm, "mid": v(176.35, 137.48) * mm, "end": v(176.52, 138.93) * mm});
            skArc(sketch, "E304", {"start": v(175.9, 136.1) * mm, "mid": v(175.71, 134.87) * mm, "end": v(175.9, 133.65) * mm});
            skArc(sketch, "E305", {"start": v(168.86, 136.8) * mm, "mid": v(171.9, 134.15) * mm, "end": v(175.9, 133.65) * mm});
            skArc(sketch, "E306", {"start": v(168.35, 136.96) * mm, "mid": v(168.37, 137.95) * mm, "end": v(168.22, 138.93) * mm});
            skArc(sketch, "E307", {"start": v(168.22, 138.93) * mm, "mid": v(167.15, 139.97) * mm, "end": v(165.73, 139.5) * mm});
            skLineSegment(sketch, "E308", {"start": v(168.86, 136.8) * mm, "end": v(168.35, 136.96) * mm});
            skArc(sketch, "E309", {"start": v(165.73, 139.5) * mm, "mid": v(165.38, 138.92) * mm, "end": v(165.03, 138.35) * mm});
            skArc(sketch, "E310", {"start": v(165.03, 138.35) * mm, "mid": v(163.5, 140.7) * mm, "end": v(161.5, 142.67) * mm});
            skArc(sketch, "E311", {"start": v(161.5, 142.67) * mm, "mid": v(160.47, 144.76) * mm, "end": v(159.37, 146.8) * mm});
            skArc(sketch, "E312", {"start": v(158.4, 151.34) * mm, "mid": v(158.55, 149) * mm, "end": v(159.37, 146.8) * mm});
            skArc(sketch, "E313", {"start": v(158.4, 151.34) * mm, "mid": v(157.27, 153.23) * mm, "end": v(155.17, 153.9) * mm});
            skArc(sketch, "E314", {"start": v(155.17, 153.9) * mm, "mid": v(153.74, 152.97) * mm, "end": v(153.22, 151.34) * mm});
            skArc(sketch, "E315", {"start": v(153.22, 151.34) * mm, "mid": v(153.34, 149.86) * mm, "end": v(153.7, 148.41) * mm});
            skArc(sketch, "E316", {"start": v(153.22, 148.41) * mm, "mid": v(151.8, 150.29) * mm, "end": v(150.1, 151.89) * mm});
            skLineSegment(sketch, "E317", {"start": v(153.7, 148.41) * mm, "end": v(153.22, 148.41) * mm});
            skArc(sketch, "E318", {"start": v(150.1, 151.89) * mm, "mid": v(147.51, 151.85) * mm, "end": v(145.78, 149.94) * mm});
            skArc(sketch, "E319", {"start": v(145.78, 149.94) * mm, "mid": v(144.6, 145.67) * mm, "end": v(144.9, 141.26) * mm});
            skArc(sketch, "E320", {"start": v(144.9, 141.26) * mm, "mid": v(145.67, 138.03) * mm, "end": v(147.28, 135.12) * mm});
            skArc(sketch, "E321", {"start": v(147.28, 135.12) * mm, "mid": v(153.44, 132.66) * mm, "end": v(159.94, 131.33) * mm});
            skArc(sketch, "E322", {"start": v(163.73, 130.18) * mm, "mid": v(161.9, 131) * mm, "end": v(159.94, 131.33) * mm});
            skArc(sketch, "E323", {"start": v(163.73, 130.18) * mm, "mid": v(169.44, 128.05) * mm, "end": v(175.36, 126.54) * mm});
            skArc(sketch, "E324", {"start": v(175.36, 126.54) * mm, "mid": v(175.7, 125.43) * mm, "end": v(176.28, 124.44) * mm});
            skArc(sketch, "E325", {"start": v(168.83, 119.88) * mm, "mid": v(172.58, 122.12) * mm, "end": v(176.28, 124.44) * mm});
            skArc(sketch, "E326", {"start": v(168.83, 119.88) * mm, "mid": v(166.42, 119.14) * mm, "end": v(164.09, 118.18) * mm});
            skArc(sketch, "E327", {"start": v(161.88, 118.18) * mm, "mid": v(162.99, 117.93) * mm, "end": v(164.09, 118.18) * mm});
            skArc(sketch, "E328", {"start": v(158.84, 117.57) * mm, "mid": v(160.4, 117.72) * mm, "end": v(161.88, 118.18) * mm});
            skArc(sketch, "E329", {"start": v(158.84, 117.57) * mm, "mid": v(157.64, 117.97) * mm, "end": v(156.38, 118.18) * mm});
            skArc(sketch, "E330", {"start": v(154.6, 117.82) * mm, "mid": v(155.5, 117.94) * mm, "end": v(156.38, 118.18) * mm});
            skArc(sketch, "E331", {"start": v(154.6, 117.82) * mm, "mid": v(150.96, 119.1) * mm, "end": v(147.27, 120.2) * mm});
            skArc(sketch, "E332", {"start": v(203.71, 134.56) * mm, "mid": v(201.46, 136.05) * mm, "end": v(199.12, 137.37) * mm});
            skArc(sketch, "E333", {"start": v(175.58, 128.24) * mm, "mid": v(175.97, 129.97) * mm, "end": v(176.04, 131.74) * mm});
            skArc(sketch, "E334", {"start": v(182.93, 132.55) * mm, "mid": v(183.27, 134.95) * mm, "end": v(183.1, 137.37) * mm});
            skArc(sketch, "E335", {"start": v(176.02, 128.15) * mm, "mid": v(176.44, 129.94) * mm, "end": v(176.56, 131.77) * mm});
            skArc(sketch, "E336", {"start": v(182.53, 132.6) * mm, "mid": v(182.67, 134.93) * mm, "end": v(182.6, 137.27) * mm});
            skArc(sketch, "E337", {"start": v(203.3, 134.2) * mm, "mid": v(201.22, 135.67) * mm, "end": v(199.02, 136.94) * mm});
            skLineSegment(sketch, "E338", {"start": v(203.71, 134.56) * mm, "end": v(203.3, 134.2) * mm});
            skLineSegment(sketch, "E339", {"start": v(199.12, 137.37) * mm, "end": v(199.02, 136.94) * mm});
            skLineSegment(sketch, "E340", {"start": v(182.93, 132.55) * mm, "end": v(182.53, 132.6) * mm});
            skLineSegment(sketch, "E341", {"start": v(183.1, 137.37) * mm, "end": v(182.6, 137.27) * mm});
            skLineSegment(sketch, "E342", {"start": v(176.56, 131.77) * mm, "end": v(176.04, 131.74) * mm});
            skLineSegment(sketch, "E343", {"start": v(176.02, 128.15) * mm, "end": v(175.58, 128.24) * mm});
            skSolve(sketch);
        }
        {
            var Q0;
            Q0=makeQuery(id+"F0.imprint","IMPRINT",FACE,{"disambiguationData":[TD([[makeQuery(id+"F0.imprint","IMPRINT",EDGE,{"derivedFrom":sQuery(id+"F0.wireOp",EDGE,"E0")}),1.0]])]});
            extrude(context, id + "F1", {"entities" : qUnion([Q0]), "depth" : 3.17 * mm, "offsetDistance" : 25.4 * mm});
        }
    });
